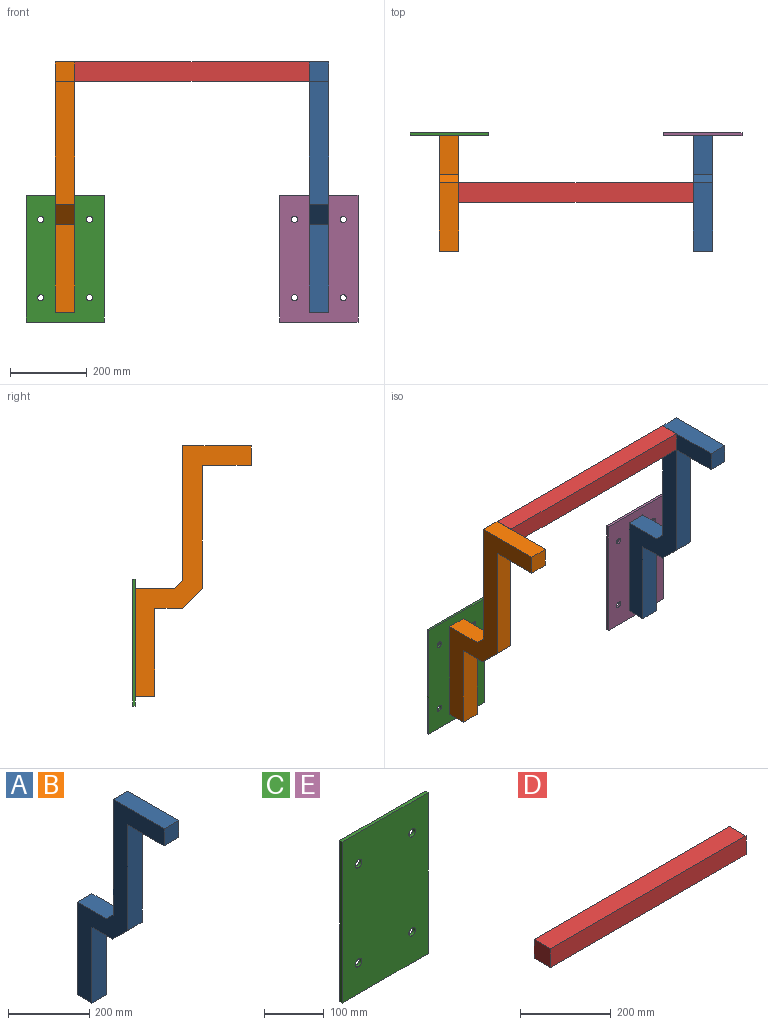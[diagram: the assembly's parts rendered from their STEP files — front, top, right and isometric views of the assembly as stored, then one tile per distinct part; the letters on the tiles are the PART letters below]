
ASSEMBLY  parts=5 mates=4
PART A: 14 faces, bbox 50.8x301.9x651.1 mm
  f0: plane 177.8x50.8mm, normal (0,0,1), area 9032.2mm2, adj f1,f11,f12,f13
  f1: plane 50.8x50.8mm, normal (0,-1,0), area 2580.6mm2, adj f0,f2,f12,f13
  f2: plane 127x50.8mm, normal (0,0,-1), area 6451.6mm2, adj f1,f3,f12,f13
  f3: plane 319.49x50.8mm, normal (0,-1,0), area 16230.2mm2, adj f2,f4,f12,f13
  f4: plane 52.21x52.21mm, normal (0,-0.71,-0.71), area 3750.8mm2, adj f3,f5,f12,f13
  f5: plane 71.84x50.8mm, normal (0,0,-1), area 3649.6mm2, adj f4,f6,f12,f13
  f6: plane 228.6x50.8mm, normal (0,-1,0), area 11612.9mm2, adj f5,f7,f12,f13
  f7: plane 50.8x50.8mm, normal (0,0,-1), area 2580.6mm2, adj f6,f8,f12,f13
  f8: plane 279.4x50.8mm, normal (0,1,0), area 14193.5mm2, adj f7,f9,f12,f13
  f9: plane 101.6x50.8mm, normal (0,0,1), area 5161.3mm2, adj f8,f10,f12,f13
  f10: plane 50.8x22.45mm, normal (0,0.71,0.71), area 1612.9mm2, adj f9,f11,f12,f13
  f11: plane 349.25x50.8mm, normal (0,1,0), area 17741.9mm2, adj f0,f10,f12,f13
  f12: plane 651.1x301.85mm, normal (1,0,0), area 44718.4mm2, adj f0,f1,f2,f3,f4,f5,f6,f7
  f13: plane 651.1x301.85mm, normal (-1,0,0), area 44718.4mm2, adj f0,f1,f2,f3,f4,f5,f6,f7
PART B: same geometry as A
PART C: 10 faces, bbox 203.2x6.4x330.2 mm
  f0: cylinder r=7.94mm len=15.88mm, axis (0,-1,0), area 316.7mm2, adj f7,f8
  f1: cylinder r=7.94mm len=15.88mm, axis (0,-1,0), area 316.7mm2, adj f7,f8
  f2: cylinder r=7.94mm len=15.88mm, axis (0,-1,0), area 316.7mm2, adj f7,f8
  f3: plane 203.2x6.35mm, normal (0,0,1), area 1290.3mm2, adj f4,f6,f7,f8
  f4: plane 330.2x6.35mm, normal (-1,0,0), area 2096.8mm2, adj f3,f5,f7,f8
  f5: plane 203.2x6.35mm, normal (0,0,-1), area 1290.3mm2, adj f4,f6,f7,f8
  f6: plane 330.2x6.35mm, normal (1,0,0), area 2096.8mm2, adj f3,f5,f7,f8
  f7: plane 330.2x203.2mm, normal (0,-1,0), area 66304.9mm2, adj f0,f1,f2,f3,f4,f5,f6,f9
  f8: plane 330.2x203.2mm, normal (0,1,0), area 66304.9mm2, adj f0,f1,f2,f3,f4,f5,f6,f9
  f9: cylinder r=7.94mm len=15.88mm, axis (0,-1,0), area 316.7mm2, adj f7,f8
PART D: 6 faces, bbox 609.6x50.8x50.8 mm
  f0: plane 609.6x50.8mm, normal (0,-1,0), area 30967.7mm2, adj f1,f3,f4,f5
  f1: plane 609.6x50.8mm, normal (0,0,-1), area 30967.7mm2, adj f0,f2,f4,f5
  f2: plane 609.6x50.8mm, normal (0,1,0), area 30967.7mm2, adj f1,f3,f4,f5
  f3: plane 609.6x50.8mm, normal (0,0,1), area 30967.7mm2, adj f0,f2,f4,f5
  f4: plane 50.8x50.8mm, normal (1,0,0), area 2580.6mm2, adj f0,f1,f2,f3
  f5: plane 50.8x50.8mm, normal (-1,0,0), area 2580.6mm2, adj f0,f1,f2,f3
PART E: same geometry as C
PLACE A t=(467.08,-194.92,250.05)mm
PLACE B t=(-193.32,-194.92,250.05)mm
PLACE C t=(-269.52,113.28,-96.25)mm
PLACE D t=(-142.52,-67.92,199.25)mm
PLACE E t=(390.88,113.28,-96.25)mm
MATE fastened D.f3 <-> A.f0  axis (0,0,1) through (467.08,-17.12,250.05)mm
MATE fastened A.f8 <-> E.f7  axis (0,1,0) through (492.48,106.93,-261.35)mm
MATE fastened C.f7 <-> B.f8  axis (0,-1,0) through (-167.92,106.93,-261.35)mm
MATE fastened D.f3 <-> B.f0  axis (0,0,1) through (-142.52,-17.12,250.05)mm
